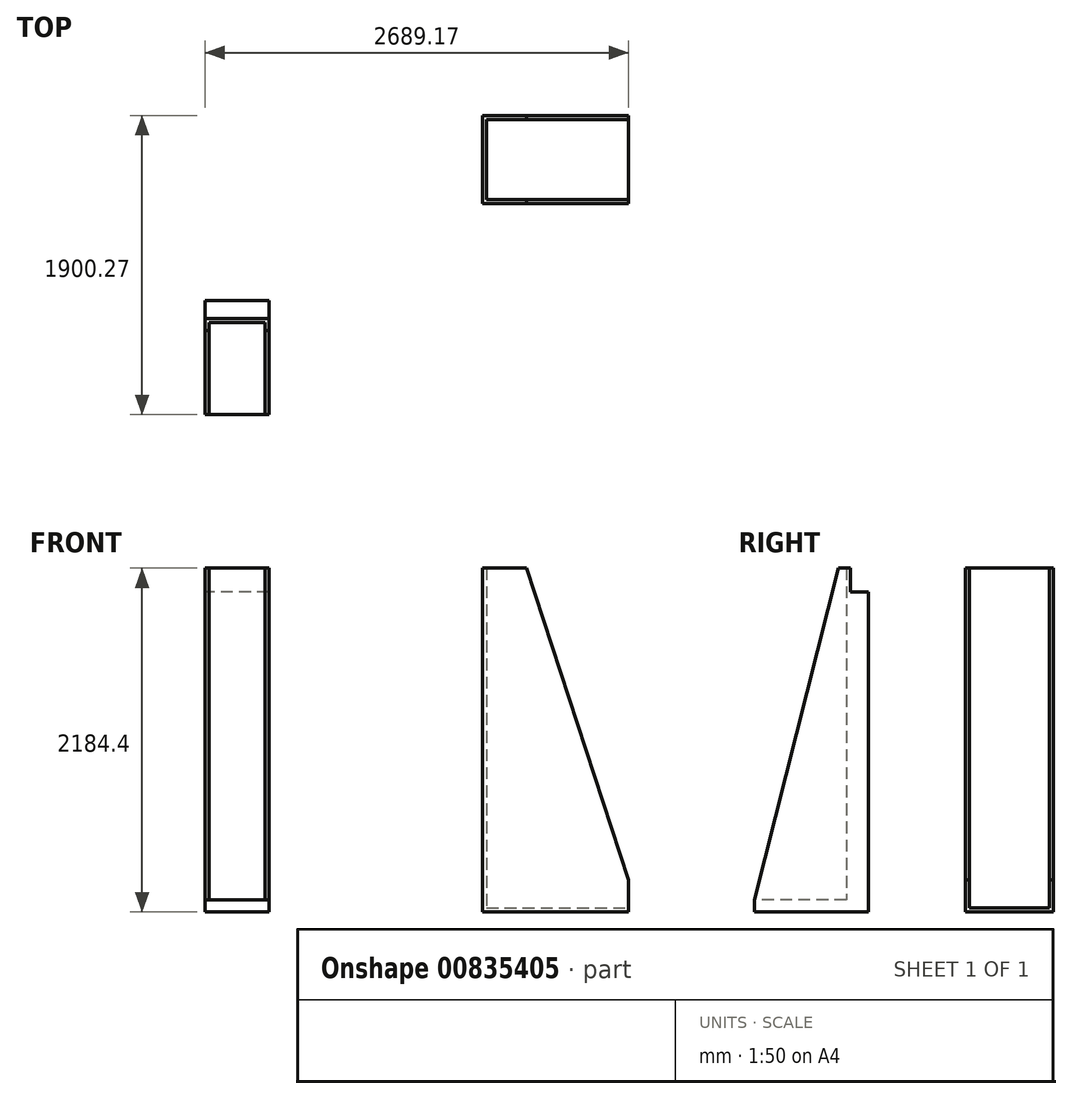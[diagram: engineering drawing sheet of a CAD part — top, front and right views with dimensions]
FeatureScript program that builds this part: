
annotation { "Feature Type Name" : "Feature", "Feature Type Description" : "" }
export const myFeature = defineFeature(function(context is Context, id is Id, definition is map)
    precondition{}
    {
        {
            var Q0;
            Q0=qCreatedBy(makeId("Top.planeOp"),FACE);
            var sketch = newSketch(context, id + "F0", { "sketchPlane" : qUnion([Q0])});
            skLineSegment(sketch, "E0.bottom", {"start": v(-217.4, -229.18) * mm, "end": v(189, -229.18) * mm});
            skLineSegment(sketch, "E0.top", {"start": v(-217.4, 380.42) * mm, "end": v(189, 380.42) * mm});
            skLineSegment(sketch, "E0.left", {"start": v(-217.4, -229.18) * mm, "end": v(-217.4, 380.42) * mm});
            skLineSegment(sketch, "E0.right", {"start": v(189, -229.18) * mm, "end": v(189, 380.42) * mm});
            skSolve(sketch);
        }
        {
            var Q0;
            Q0=makeQuery(id+"F0.imprint","IMPRINT",FACE,{"disambiguationData":[TD([[makeQuery(id+"F0.imprint","IMPRINT",EDGE,{"derivedFrom":sQuery(id+"F0.wireOp",EDGE,"E0.bottom")}),1.0]])]});
            extrude(context, id + "F1", {"entities" : qUnion([Q0]), "depth" : 2184.4 * mm, "offsetDistance" : 25.4 * mm});
        }
        {
            var Q0;
            Q0=makeQuery(id+"F1.opExtrude","SWEPT_FACE",FACE,{"disambiguationData":[OSD([sQuery(id+"F0.wireOp",EDGE,"E0.right")])]});
            var sketch = newSketch(context, id + "F2", { "sketchPlane" : qUnion([Q0])});
            skLineSegment(sketch, "E1", {"start": v(-229.18, 76.2) * mm, "end": v(304.22, 2184.4) * mm});
            skSolve(sketch);
        }
        {
            var Q0;
            Q0=makeQuery(id+"F1.opExtrude","SWEPT_FACE",FACE,{"disambiguationData":[OSD([sQuery(id+"F0.wireOp",EDGE,"E0.bottom")])]});
            var sketch = newSketch(context, id + "F3", { "sketchPlane" : qUnion([Q0])});
            skLineSegment(sketch, "E2.bottom", {"start": v(-192, 2184.4) * mm, "end": v(163.6, 2184.4) * mm});
            skLineSegment(sketch, "E2.top", {"start": v(-192, 76.2) * mm, "end": v(163.6, 76.2) * mm});
            skLineSegment(sketch, "E2.left", {"start": v(-192, 2184.4) * mm, "end": v(-192, 76.2) * mm});
            skLineSegment(sketch, "E2.right", {"start": v(163.6, 2184.4) * mm, "end": v(163.6, 76.2) * mm});
            skSolve(sketch);
        }
        {
            var Q0;
            Q0=makeQuery(id+"F3.imprint","IMPRINT",FACE,{"disambiguationData":[TD([[makeQuery(id+"F3.imprint","IMPRINT",EDGE,{"derivedFrom":sQuery(id+"F3.wireOp",EDGE,"E2.bottom")}),-1.0]])]});
            extrude(context, id + "F4", {"entities" : qUnion([Q0]), "operationType" : NewBodyOperationType.REMOVE, "oppositeDirection" : true, "depth" : 584.2 * mm, "offsetDistance" : 25.4 * mm});
        }
        {
            var Q0;
            {var subQ0=sQuery(id+"F2.wireOp",EDGE,"E1");Q0=makeQuery(id+"F2.imprint","IMPRINT",FACE,{"disambiguationData":[TD([[makeQuery(id+"F2.imprint","IMPRINT",EDGE,{"derivedFrom":subQ0}),1.0]])]});}
            extrude(context, id + "F5", {"entities" : qUnion([Q0]), "operationType" : NewBodyOperationType.REMOVE, "oppositeDirection" : true, "depth" : 406.4 * mm, "offsetDistance" : 25.4 * mm});
        }
        {
            var Q0;
            Q0=makeQuery(id+"F1.opExtrude","SWEPT_FACE",FACE,{"disambiguationData":[OSD([sQuery(id+"F0.wireOp",EDGE,"E0.top")])]});
            var sketch = newSketch(context, id + "F6", { "sketchPlane" : qUnion([Q0])});
            skLineSegment(sketch, "E3.bottom", {"start": v(-189, 2032) * mm, "end": v(217.4, 2032) * mm});
            skLineSegment(sketch, "E3.top", {"start": v(-189, 0) * mm, "end": v(217.4, 0) * mm});
            skLineSegment(sketch, "E3.left", {"start": v(-189, 2032) * mm, "end": v(-189, 0) * mm});
            skLineSegment(sketch, "E3.right", {"start": v(217.4, 2032) * mm, "end": v(217.4, 0) * mm});
            skSolve(sketch);
        }
        {
            var Q0;
            Q0=makeQuery(id+"F6.imprint","IMPRINT",FACE,{"disambiguationData":[TD([[makeQuery(id+"F6.imprint","IMPRINT",EDGE,{"derivedFrom":sQuery(id+"F6.wireOp",EDGE,"E3.bottom")}),-1.0]])]});
            extrude(context, id + "F7", {"entities" : qUnion([Q0]), "operationType" : NewBodyOperationType.ADD, "depth" : 114.3 * mm, "offsetDistance" : 25.4 * mm});
        }
        {
            var Q0;
            Q0=qCreatedBy(makeId("Top.planeOp"),FACE);
            var sketch = newSketch(context, id + "F8", { "sketchPlane" : qUnion([Q0])});
            skLineSegment(sketch, "E4.bottom", {"start": v(1544.66, 1112.3) * mm, "end": v(2471.76, 1112.3) * mm});
            skLineSegment(sketch, "E4.top", {"start": v(1544.66, 1671.1) * mm, "end": v(2471.76, 1671.1) * mm});
            skLineSegment(sketch, "E4.left", {"start": v(1544.66, 1112.3) * mm, "end": v(1544.66, 1671.1) * mm});
            skLineSegment(sketch, "E4.right", {"start": v(2471.76, 1112.3) * mm, "end": v(2471.76, 1671.1) * mm});
            skSolve(sketch);
        }
        {
            var Q0;
            Q0=makeQuery(id+"F8.imprint","IMPRINT",FACE,{"disambiguationData":[TD([[makeQuery(id+"F8.imprint","IMPRINT",EDGE,{"derivedFrom":sQuery(id+"F8.wireOp",EDGE,"E4.bottom")}),1.0]])]});
            extrude(context, id + "F9", {"entities" : qUnion([Q0]), "depth" : 2184.4 * mm, "offsetDistance" : 25.4 * mm});
        }
        {
            var Q0;
            Q0=makeQuery(id+"F9.opExtrude","SWEPT_FACE",FACE,{"disambiguationData":[OSD([sQuery(id+"F8.wireOp",EDGE,"E4.right")])]});
            var sketch = newSketch(context, id + "F10", { "sketchPlane" : qUnion([Q0])});
            skLineSegment(sketch, "E5.bottom", {"start": v(1137.7, 2184.4) * mm, "end": v(1645.7, 2184.4) * mm});
            skLineSegment(sketch, "E5.top", {"start": v(1137.7, 25.4) * mm, "end": v(1645.7, 25.4) * mm});
            skLineSegment(sketch, "E5.left", {"start": v(1137.7, 2184.4) * mm, "end": v(1137.7, 25.4) * mm});
            skLineSegment(sketch, "E5.right", {"start": v(1645.7, 2184.4) * mm, "end": v(1645.7, 25.4) * mm});
            skSolve(sketch);
        }
        {
            var Q0;
            Q0=makeQuery(id+"F10.imprint","IMPRINT",FACE,{"disambiguationData":[TD([[makeQuery(id+"F10.imprint","IMPRINT",EDGE,{"derivedFrom":sQuery(id+"F10.wireOp",EDGE,"E5.bottom")}),-1.0]])]});
            extrude(context, id + "F11", {"entities" : qUnion([Q0]), "operationType" : NewBodyOperationType.REMOVE, "oppositeDirection" : true, "depth" : 901.7 * mm, "offsetDistance" : 25.4 * mm});
        }
        {
            var Q0;
            Q0=makeQuery(id+"F9.opExtrude","SWEPT_FACE",FACE,{"disambiguationData":[OSD([sQuery(id+"F8.wireOp",EDGE,"E4.top")])]});
            var sketch = newSketch(context, id + "F12", { "sketchPlane" : qUnion([Q0])});
            skLineSegment(sketch, "E6", {"start": v(-2471.76, 203.2) * mm, "end": v(-1824.06, 2184.4) * mm});
            skSolve(sketch);
        }
        {
            var Q0;
            {var subQ0=sQuery(id+"F12.wireOp",EDGE,"E6");Q0=makeQuery(id+"F12.imprint","IMPRINT",FACE,{"disambiguationData":[TD([[makeQuery(id+"F12.imprint","IMPRINT",EDGE,{"derivedFrom":subQ0}),1.0]])]});}
            extrude(context, id + "F13", {"entities" : qUnion([Q0]), "operationType" : NewBodyOperationType.REMOVE, "oppositeDirection" : true, "depth" : 558.8 * mm, "offsetDistance" : 25.4 * mm});
        }
    });
